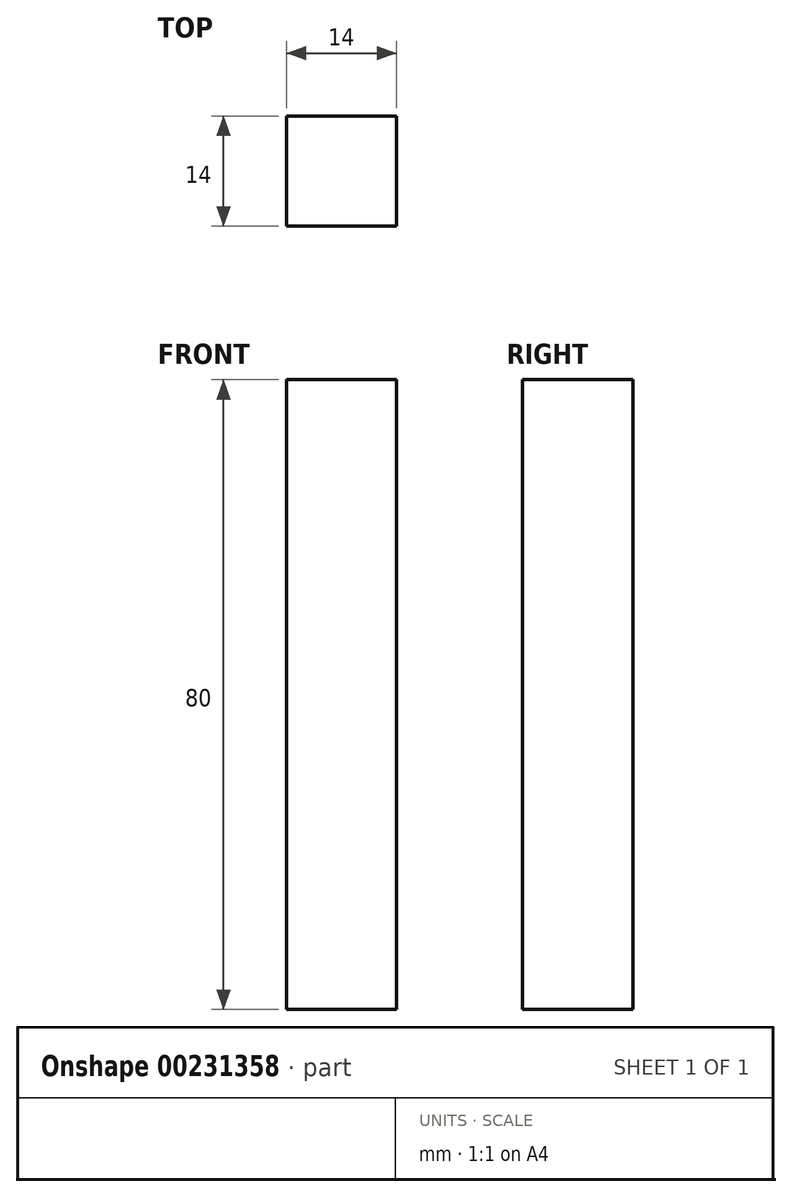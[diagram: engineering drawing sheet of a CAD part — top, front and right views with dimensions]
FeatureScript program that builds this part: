
annotation { "Feature Type Name" : "Feature", "Feature Type Description" : "" }
export const myFeature = defineFeature(function(context is Context, id is Id, definition is map)
    precondition{}
    {
        {
            var Q0;
            Q0=qCreatedBy(makeId("Top.planeOp"),FACE);
            var sketch = newSketch(context, id + "F0", { "sketchPlane" : qUnion([Q0])});
            skLineSegment(sketch, "E0.bottom", {"start": v(7, -7) * mm, "end": v(-7, -7) * mm});
            skLineSegment(sketch, "E0.top", {"start": v(7, 7) * mm, "end": v(-7, 7) * mm});
            skLineSegment(sketch, "E0.left", {"start": v(7, -7) * mm, "end": v(7, 7) * mm});
            skLineSegment(sketch, "E0.right", {"start": v(-7, -7) * mm, "end": v(-7, 7) * mm});
            skPoint(sketch, "E0.middle", {"position": v(0, 0) * mm});
            skSolve(sketch);
        }
        {
            var Q0;
            Q0 = qSketchRegion(id + "F0", true);
            extrude(context, id + "F1", {"entities" : qUnion([Q0]), "depth" : 80 * mm});
        }
    });
